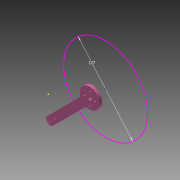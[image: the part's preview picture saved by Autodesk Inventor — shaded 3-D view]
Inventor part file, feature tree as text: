
AUTODESK INVENTOR PART (.ipt)
format: ipt  version: 2015 (Build 190159000, 159)  size: 101,888 bytes
history: native  units: mm
features: other x2, extrude x1, sketch x1
ambient origin geometry x8: Origin, YZ Plane, XZ Plane, XY Plane, X Axis, Y Axis, Z Axis, Center Point
bodies: Body1 (feature_tree)
feature tree (4):
  extrude  "Arm 4 mm"  Depth=3.0mm
  other  "Simulerar Motor"
  other  "Propeller"
  sketch  "Sketch1"  dims[d2=3.0mm d3=3.0mm d4=3.0mm d6=6.0mm d10=2.0mm d11=4.0mm d12=0.0mm d13=20.0mm d14=127.0mm]
